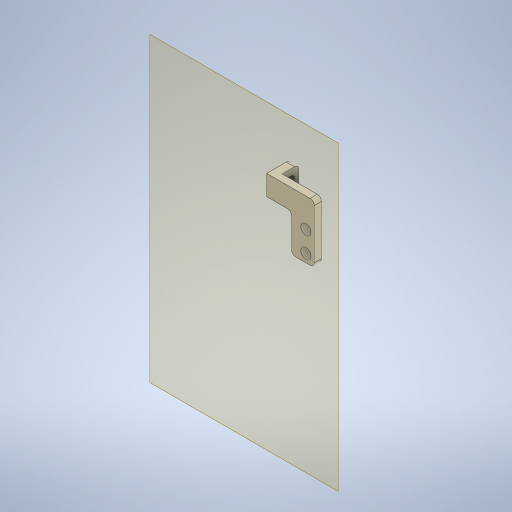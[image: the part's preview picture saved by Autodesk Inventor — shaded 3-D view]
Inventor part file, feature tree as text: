
AUTODESK INVENTOR PART (.ipt)
format: ipt  version: 2024 (Build 280153000, 153)  size: 637,952 bytes
history: native  units: mm
features: other x3, sketch x1, plane x1
ambient origin geometry x8: Origin, YZ Plane, XZ Plane, XY Plane, X Axis, Y Axis, Z Axis, Center Point
bodies: Solid1 (feature_tree)
feature tree (5):
  other  "midle-tensioner.ipt"
  other  "Solid1::midle-tensioner.ipt"
  other  "TaggingFeature1"
  sketch  "Sketch1"  dims[d0=10.0mm]
  plane  "Work Plane1"
